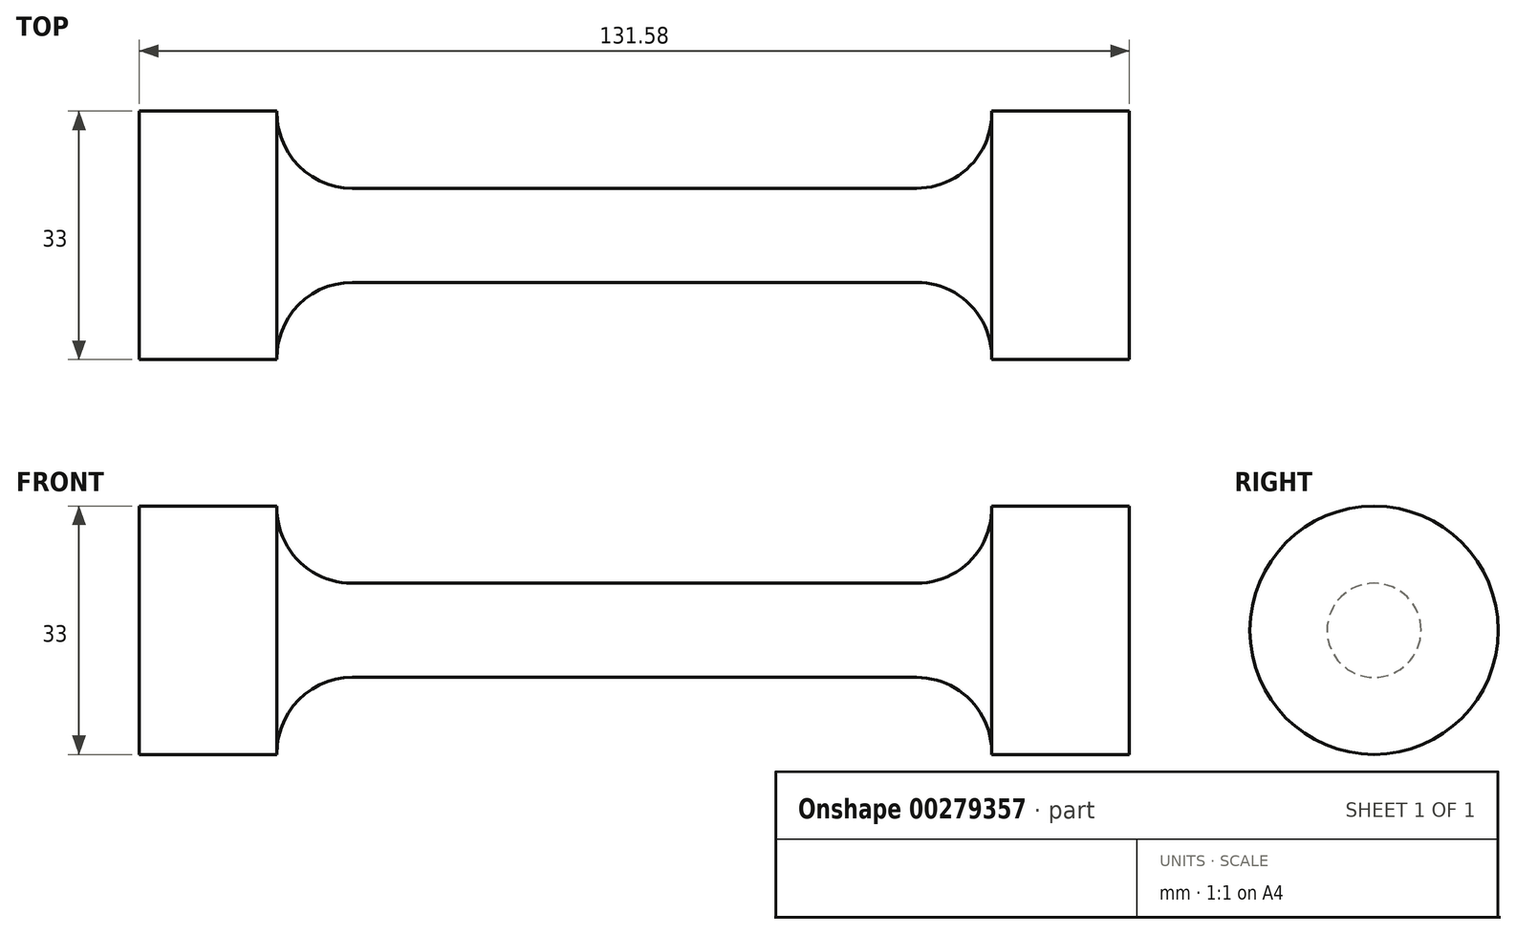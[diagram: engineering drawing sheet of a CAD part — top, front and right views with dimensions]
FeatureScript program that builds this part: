
annotation { "Feature Type Name" : "Feature", "Feature Type Description" : "" }
export const myFeature = defineFeature(function(context is Context, id is Id, definition is map)
    precondition{}
    {
        {
            var Q0;
            Q0=qCreatedBy(makeId("Front.planeOp"),FACE);
            var sketch = newSketch(context, id + "F0", { "sketchPlane" : qUnion([Q0])});
            skLineSegment(sketch, "E0", {"start": v(0, 6.25) * mm, "end": v(37.5, 6.25) * mm});
            skArc(sketch, "E1", {"start": v(37.5, 6.25) * mm, "mid": v(44.66, 9.27) * mm, "end": v(47.5, 16.5) * mm});
            skLineSegment(sketch, "E2", {"start": v(47.5, 16.5) * mm, "end": v(65.79, 16.5) * mm});
            skLineSegment(sketch, "E3", {"start": v(65.79, 16.5) * mm, "end": v(65.79, 0) * mm});
            skLineSegment(sketch, "E4.MirrorCS", {"start": v(0, 6.25) * mm, "end": v(-37.5, 6.25) * mm});
            skLineSegment(sketch, "E5.MirrorCS", {"start": v(-65.79, 16.5) * mm, "end": v(-65.79, 0) * mm});
            skLineSegment(sketch, "E6.MirrorCS", {"start": v(-47.5, 16.5) * mm, "end": v(-65.79, 16.5) * mm});
            skArc(sketch, "E7.MirrorCS", {"start": v(-37.5, 6.25) * mm, "mid": v(-44.66, 9.27) * mm, "end": v(-47.5, 16.5) * mm});
            skLineSegment(sketch, "E8", {"start": v(-65.79, 0) * mm, "end": v(65.79, 0) * mm});
            skSolve(sketch);
        }
        {
            var Q0;
            Q0=makeQuery(id+"F0.imprint","IMPRINT",FACE,{"disambiguationData":[TD([[makeQuery(id+"F0.imprint","IMPRINT",EDGE,{"derivedFrom":sQuery(id+"F0.wireOp",EDGE,"E0")}),-1.0]])]});
            var Q1;
            Q1=sQuery(id+"F0.wireOp",EDGE,"E8");
            revolve(context, id + "F1", {"entities" : qUnion([Q0]), "axis" : qUnion([Q1]), "revolveType" : RevolveType.FULL});
        }
    });
